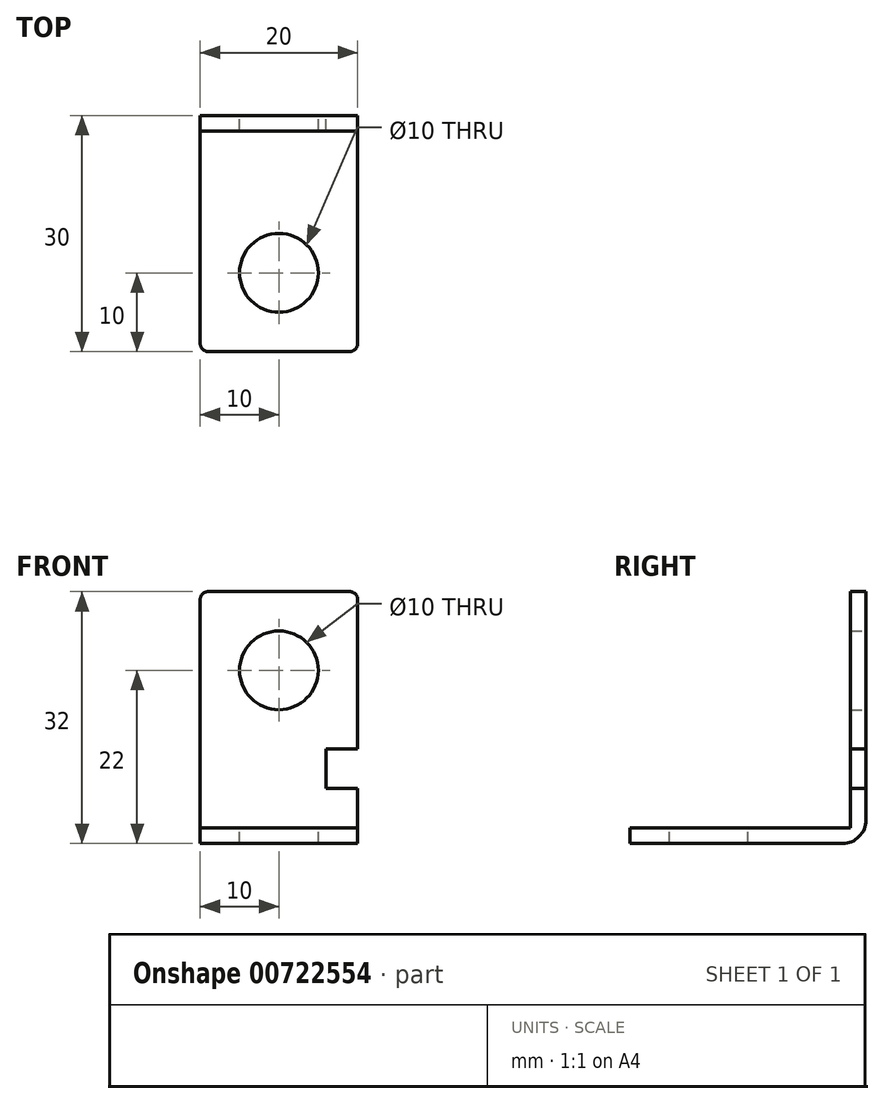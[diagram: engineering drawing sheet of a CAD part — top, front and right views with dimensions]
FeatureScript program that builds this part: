
annotation { "Feature Type Name" : "Feature", "Feature Type Description" : "" }
export const myFeature = defineFeature(function(context is Context, id is Id, definition is map)
    precondition{}
    {
        {
            var Q0;
            Q0=qCreatedBy(makeId("Front.planeOp"),FACE);
            var sketch = newSketch(context, id + "F0", { "sketchPlane" : qUnion([Q0])});
            skLineSegment(sketch, "E0.bottom", {"start": v(-10, 15) * mm, "end": v(10, 15) * mm});
            skLineSegment(sketch, "E0.top", {"start": v(-10, -15) * mm, "end": v(10, -15) * mm});
            skLineSegment(sketch, "E0.left", {"start": v(-10, 15) * mm, "end": v(-10, -15) * mm});
            skLineSegment(sketch, "E0.right", {"start": v(10, 15) * mm, "end": v(10, -15) * mm});
            skPoint(sketch, "E0.middle", {"position": v(0, 0) * mm});
            skCircle(sketch, "E1", {"center": v(0, 5) * mm, "radius": 5 * mm});
            skLineSegment(sketch, "E2.bottom", {"start": v(10, -5) * mm, "end": v(6, -5) * mm});
            skLineSegment(sketch, "E2.top", {"start": v(10, -10) * mm, "end": v(6, -10) * mm});
            skLineSegment(sketch, "E2.left", {"start": v(10, -5) * mm, "end": v(10, -10) * mm});
            skLineSegment(sketch, "E2.right", {"start": v(6, -5) * mm, "end": v(6, -10) * mm});
            skSolve(sketch);
        }
        {
            var Q0;
            {var subQ1=sQuery(id+"F0.wireOp",EDGE,"E0.bottom");Q0=makeQuery(id+"F0.imprint","IMPRINT",FACE,{"disambiguationData":[TD([[makeQuery(id+"F0.imprint","IMPRINT",EDGE,{"derivedFrom":subQ1}),-1.0]])]});}
            extrude(context, id + "F1", {"entities" : qUnion([Q0]), "depth" : 2 * mm, "offsetDistance" : 25 * mm});
        }
        {
            var Q0;
            Q0=makeQuery(id+"F1.opExtrude","CAP_FACE",FACE,{"disambiguationData":[OSD([sQuery(id+"F0.wireOp",EDGE,"E0.bottom"),sQuery(id+"F0.wireOp",EDGE,"E0.top"),sQuery(id+"F0.wireOp",EDGE,"E0.left"),sQuery(id+"F0.wireOp",EDGE,"E0.right"),sQuery(id+"F0.wireOp",EDGE,"E1"),sQuery(id+"F0.wireOp",EDGE,"E2.bottom"),sQuery(id+"F0.wireOp",EDGE,"E2.top"),sQuery(id+"F0.wireOp",EDGE,"E2.right")])],"isStart":true});
            var sketch = newSketch(context, id + "F2", { "sketchPlane" : qUnion([Q0])});
            skLineSegment(sketch, "E3.bottom", {"start": v(-10, -15) * mm, "end": v(10, -15) * mm});
            skLineSegment(sketch, "E3.top", {"start": v(-10, -17) * mm, "end": v(10, -17) * mm});
            skLineSegment(sketch, "E3.left", {"start": v(10, -17) * mm, "end": v(10, -15) * mm});
            skLineSegment(sketch, "E3.right", {"start": v(-10, -17) * mm, "end": v(-10, -15) * mm});
            skSolve(sketch);
        }
        {
            var Q0;
            Q0 = qSketchRegion(id + "F2", true);
            extrude(context, id + "F3", {"entities" : qUnion([Q0]), "operationType" : NewBodyOperationType.ADD, "oppositeDirection" : true, "depth" : 30 * mm, "offsetDistance" : 25 * mm});
        }
        {
            var Q0;
            Q0=makeQuery(id+"F1.opExtrude","CAP_EDGE",EDGE,{"disambiguationData":[OSD([sQuery(id+"F0.wireOp",EDGE,"E0.top")])],"isStart":false});
            var Q1;
            Q1=makeQuery(id+"F3.opExtrude","CAP_EDGE",EDGE,{"disambiguationData":[OSD([sQuery(id+"F2.wireOp",EDGE,"E3.top")])],"isStart":true});
            fillet(context, id + "F4", {"entities" : qUnion([Q0, Q1]), "radius" : 3 * mm, "tangentPropagation" : true, "allowEdgeOverflow" : false});
        }
        {
            var Q0;
            Q0=makeQuery(id+"F3.opExtrude","SWEPT_FACE",FACE,{"disambiguationData":[OSD([sQuery(id+"F2.wireOp",EDGE,"E3.bottom")])]});
            var sketch = newSketch(context, id + "F5", { "sketchPlane" : qUnion([Q0])});
            skCircle(sketch, "E4", {"center": v(0, -20) * mm, "radius": 5 * mm});
            skSolve(sketch);
        }
        {
            var Q0;
            Q0 = qSketchRegion(id + "F5", true);
            extrude(context, id + "F6", {"entities" : qUnion([Q0]), "operationType" : NewBodyOperationType.REMOVE, "endBound" : BoundingType.THROUGH_ALL, "oppositeDirection" : true, "depth" : 25 * mm, "offsetDistance" : 25 * mm});
        }
        {
            var Q0;
            Q0=makeQuery(id+"F1.opExtrude","SWEPT_EDGE",EDGE,{"disambiguationData":[OSD([sQuery(id+"F0.wireOp",EDGE,"E0.bottom"),sQuery(id+"F0.wireOp",EDGE,"E0.left")])]});
            var Q1;
            Q1=makeQuery(id+"F1.opExtrude","SWEPT_EDGE",EDGE,{"disambiguationData":[OSD([sQuery(id+"F0.wireOp",EDGE,"E0.bottom"),sQuery(id+"F0.wireOp",EDGE,"E0.right")])]});
            var Q2;
            Q2=makeQuery(id+"F3.opExtrude","CAP_EDGE",EDGE,{"disambiguationData":[OSD([sQuery(id+"F2.wireOp",EDGE,"E3.left")])],"isStart":false});
            var Q3;
            Q3=makeQuery(id+"F3.opExtrude","CAP_EDGE",EDGE,{"disambiguationData":[OSD([sQuery(id+"F2.wireOp",EDGE,"E3.right")])],"isStart":false});
            fillet(context, id + "F7", {"entities" : qUnion([Q0, Q1, Q2, Q3]), "radius" : 1 * mm, "tangentPropagation" : true, "allowEdgeOverflow" : false});
        }
    });
